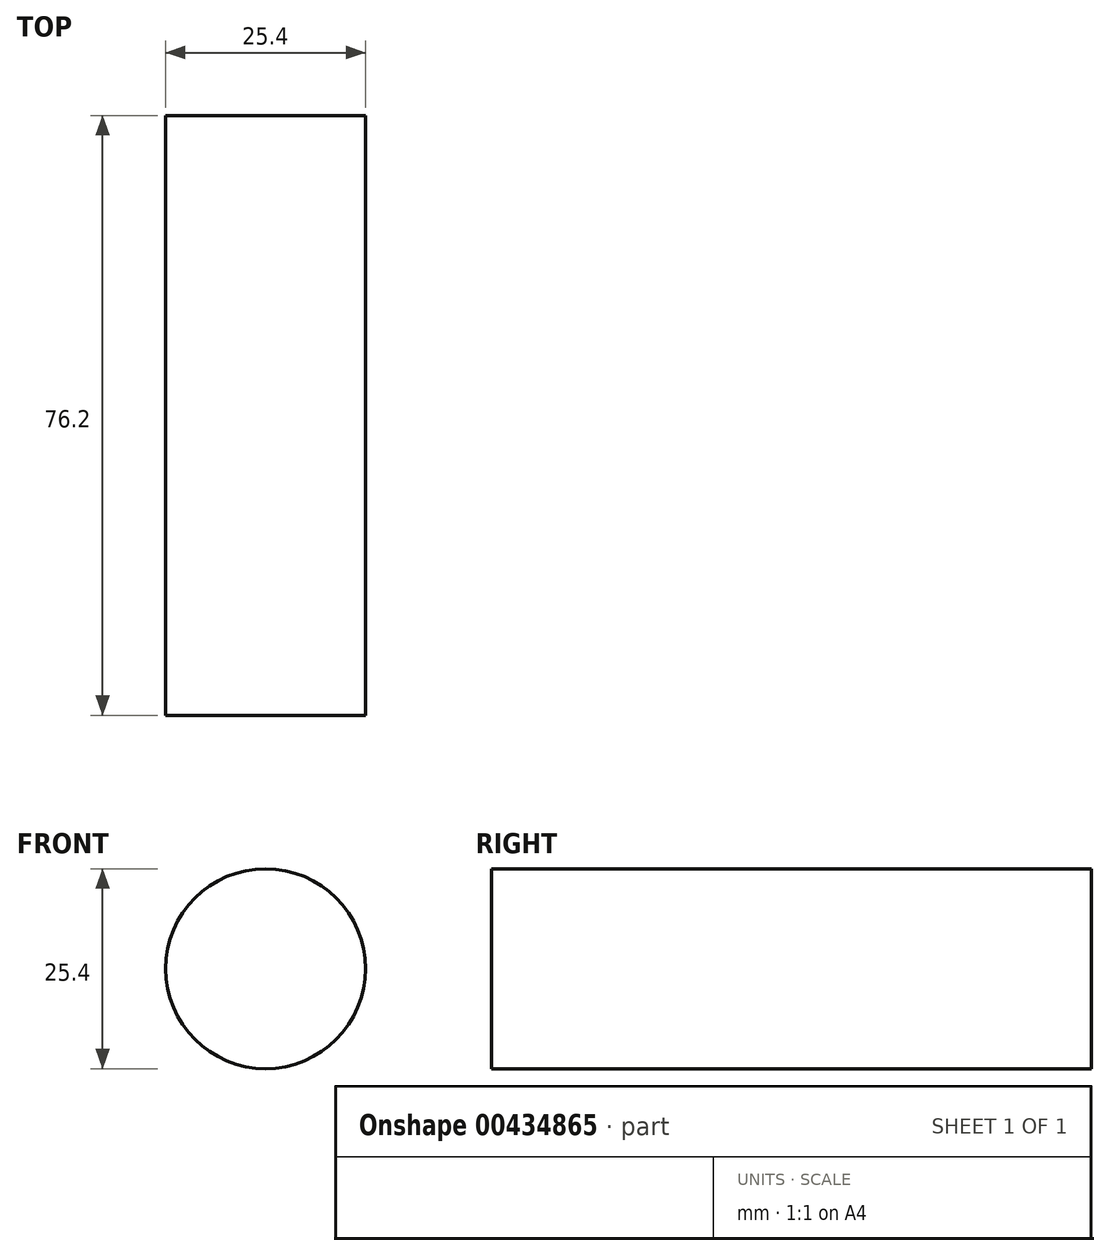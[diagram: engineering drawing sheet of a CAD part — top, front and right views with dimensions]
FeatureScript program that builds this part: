
annotation { "Feature Type Name" : "Feature", "Feature Type Description" : "" }
export const myFeature = defineFeature(function(context is Context, id is Id, definition is map)
    precondition{}
    {
        {
            var Q0;
            Q0=qCreatedBy(makeId("Front.planeOp"),FACE);
            var sketch = newSketch(context, id + "F0", { "sketchPlane" : qUnion([Q0])});
            skCircle(sketch, "E0", {"center": v(-10.5, 15.85) * mm, "radius": 12.7 * mm});
            skSolve(sketch);
        }
        {
            var Q0;
            Q0 = qSketchRegion(id + "F0", true);
            extrude(context, id + "F1", {"entities" : qUnion([Q0]), "depth" : 76.2 * mm});
        }
    });
